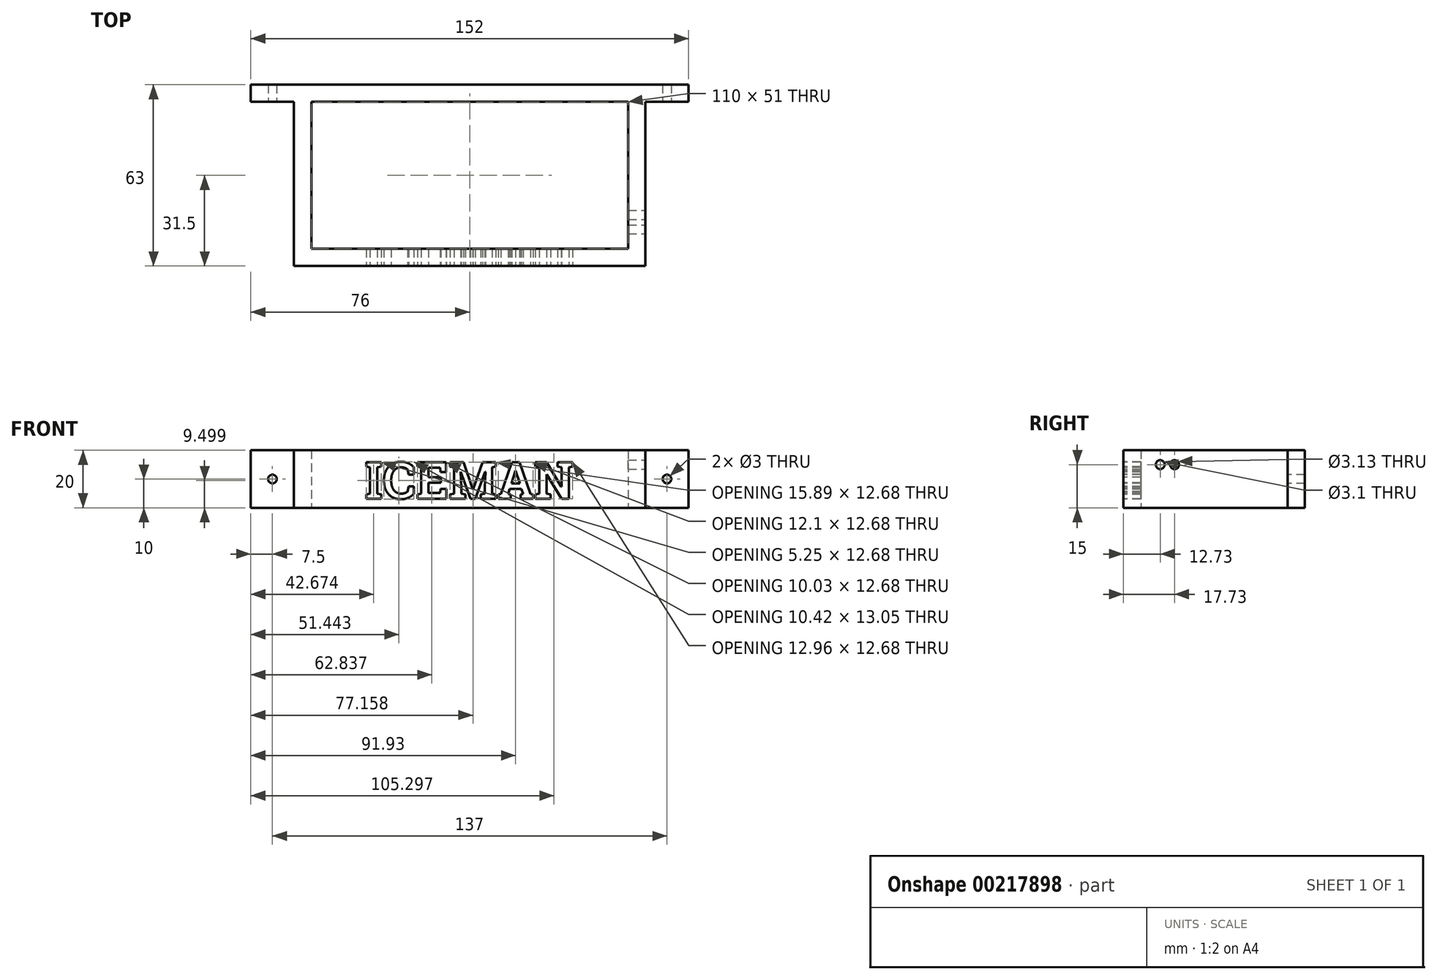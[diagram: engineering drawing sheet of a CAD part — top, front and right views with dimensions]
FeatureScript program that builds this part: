
annotation { "Feature Type Name" : "Feature", "Feature Type Description" : "" }
export const myFeature = defineFeature(function(context is Context, id is Id, definition is map)
    precondition{}
    {
        {
            var Q0;
            Q0=qCreatedBy(makeId("Top.planeOp"),FACE);
            var sketch = newSketch(context, id + "F0", { "sketchPlane" : qUnion([Q0])});
            skLineSegment(sketch, "E0.bottom", {"start": v(-61, 31.5) * mm, "end": v(61, 31.5) * mm});
            skLineSegment(sketch, "E0.top", {"start": v(-61, -31.5) * mm, "end": v(61, -31.5) * mm});
            skLineSegment(sketch, "E0.left", {"start": v(-61, 31.5) * mm, "end": v(-61, -31.5) * mm});
            skLineSegment(sketch, "E0.right", {"start": v(61, 31.5) * mm, "end": v(61, -31.5) * mm});
            skPoint(sketch, "E0.middle", {"position": v(0, 0) * mm});
            skSolve(sketch);
        }
        {
            var Q0;
            Q0=qSketchRegion(id+"F0",true);
            extrude(context, id + "F1", {"entities" : qUnion([Q0]), "depth" : 6 * mm});
        }
        {
            var Q0;
            Q0=makeQuery(id+"F1.opExtrude","CAP_FACE",FACE,{"disambiguationData":[OSD([sQuery(id+"F0.wireOp",EDGE,"E0.bottom"),sQuery(id+"F0.wireOp",EDGE,"E0.top"),sQuery(id+"F0.wireOp",EDGE,"E0.left"),sQuery(id+"F0.wireOp",EDGE,"E0.right")])],"isStart":false});
            var sketch = newSketch(context, id + "F2", { "sketchPlane" : qUnion([Q0])});
            skLineSegment(sketch, "E1", {"start": v(-55, 25.5) * mm, "end": v(-55, -25.5) * mm});
            skLineSegment(sketch, "E2", {"start": v(-55, -25.5) * mm, "end": v(55, -25.5) * mm});
            skLineSegment(sketch, "E3", {"start": v(55, 25.5) * mm, "end": v(-55, 25.5) * mm});
            skLineSegment(sketch, "E4", {"start": v(55, 25.5) * mm, "end": v(55, -25.5) * mm});
            skPoint(sketch, "E5.orphan", {"position": v(55, -31.5) * mm});
            skLineSegment(sketch, "E6.bottom", {"start": v(-61, 31.5) * mm, "end": v(61, 31.5) * mm});
            skLineSegment(sketch, "E6.top", {"start": v(-61, -31.5) * mm, "end": v(61, -31.5) * mm});
            skLineSegment(sketch, "E6.left", {"start": v(-61, 31.5) * mm, "end": v(-61, -31.5) * mm});
            skLineSegment(sketch, "E6.right", {"start": v(61, 31.5) * mm, "end": v(61, -31.5) * mm});
            skSolve(sketch);
        }
        {
            var Q0;
            Q0=qSketchRegion(id+"F2",true);
            extrude(context, id + "F3", {"entities" : qUnion([Q0]), "operationType" : NewBodyOperationType.ADD, "depth" : 66 * mm});
        }
        {
            var Q0;
            Q0=makeQuery(id+"F3.boolean.opBoolean","MERGE",FACE,{"derivedFrom":[makeQuery(id+"F1.opExtrude","SWEPT_FACE",FACE,{"disambiguationData":[OSD([sQuery(id+"F0.wireOp",EDGE,"E0.top")])]}),makeQuery(id+"F3.opExtrude","SWEPT_FACE",FACE,{"disambiguationData":[OSD([sQuery(id+"F2.wireOp",EDGE,"E6.top")])]})]});
            var sketch = newSketch(context, id + "F4", { "sketchPlane" : qUnion([Q0])});
            skLineSegment(sketch, "E7.bottom", {"start": v(48, 30.5) * mm, "end": v(20.38, 30.5) * mm});
            skLineSegment(sketch, "E7.top", {"start": v(48, 9) * mm, "end": v(20.38, 9) * mm});
            skLineSegment(sketch, "E7.left", {"start": v(48, 30.5) * mm, "end": v(48, 9) * mm});
            skLineSegment(sketch, "E7.right", {"start": v(20.38, 30.5) * mm, "end": v(20.38, 9) * mm});
            skLineSegment(sketch, "E8.bottom", {"start": v(-48, 30.5) * mm, "end": v(-21, 30.5) * mm});
            skLineSegment(sketch, "E8.top", {"start": v(-48, 12.5) * mm, "end": v(-21, 12.5) * mm});
            skLineSegment(sketch, "E8.left", {"start": v(-48, 30.5) * mm, "end": v(-48, 12.5) * mm});
            skLineSegment(sketch, "E8.right", {"start": v(-21, 30.5) * mm, "end": v(-21, 12.5) * mm});
            skText(sketch, "E9", { "text": "ICEMAN", "fontName": "RobotoSlab-Bold.ttf"});
            const initialGuessF4  = {"E9": [-0.03643, 0.04416, 1, 0, 0.01284]};
            skSetInitialGuess(sketch, initialGuessF4);
            skSolve(sketch);
        }
        {
            var Q0;
            Q0=qSketchRegion(id+"F4",true);
            extrude(context, id + "F5", {"entities" : qUnion([Q0]), "operationType" : NewBodyOperationType.REMOVE, "oppositeDirection" : true, "depth" : 6 * mm});
        }
        {
            var Q0;
            Q0=makeQuery(id+"F1.opExtrude","CAP_FACE",FACE,{"disambiguationData":[OSD([sQuery(id+"F0.wireOp",EDGE,"E0.bottom"),sQuery(id+"F0.wireOp",EDGE,"E0.top"),sQuery(id+"F0.wireOp",EDGE,"E0.left"),sQuery(id+"F0.wireOp",EDGE,"E0.right")])],"isStart":true});
            var sketch = newSketch(context, id + "F6", { "sketchPlane" : qUnion([Q0])});
            skPoint(sketch, "E10.bottom.start.orphan", {"position": v(42.45, 0) * mm});
            skText(sketch, "E11", { "text": "ICEMAN", "fontName": "OpenSans-BoldItalic.ttf"});
            const initialGuessF6  = {"E11": [-0.06005, -0.01114, 1, 0, 0.02254]};
            skSetInitialGuess(sketch, initialGuessF6);
            skSolve(sketch);
        }
        {
            var Q0;
            Q0=qSketchRegion(id+"F6",true);
            extrude(context, id + "F7", {"entities" : qUnion([Q0]), "operationType" : NewBodyOperationType.REMOVE, "oppositeDirection" : true, "depth" : 6 * mm});
        }
        {
            var Q0;
            Q0=makeQuery(id+"F3.boolean.opBoolean","MERGE",FACE,{"derivedFrom":[makeQuery(id+"F1.opExtrude","SWEPT_FACE",FACE,{"disambiguationData":[OSD([sQuery(id+"F0.wireOp",EDGE,"E0.right")])]}),makeQuery(id+"F3.opExtrude","SWEPT_FACE",FACE,{"disambiguationData":[OSD([sQuery(id+"F2.wireOp",EDGE,"E6.right")])]})]});
            var sketch = newSketch(context, id + "F8", { "sketchPlane" : qUnion([Q0])});
            skCircle(sketch, "E12", {"center": v(-18.77, 56) * mm, "radius": 1.55 * mm});
            skLineSegment(sketch, "E13", {"start": v(-18.77, 56) * mm, "end": v(33.66, 56) * mm, "construction": true});
            skCircle(sketch, "E14", {"center": v(-13.77, 56) * mm, "radius": 1.55 * mm, "construction": true});
            skCircle(sketch, "E15", {"center": v(-13.77, 56) * mm, "radius": 1.56 * mm});
            skSolve(sketch);
        }
        {
            var Q0;
            Q0=qSketchRegion(id+"F8",true);
            extrude(context, id + "F9", {"entities" : qUnion([Q0]), "operationType" : NewBodyOperationType.REMOVE, "oppositeDirection" : true, "depth" : 6 * mm});
        }
        {
            var Q0;
            Q0=makeQuery(id+"F3.boolean.opBoolean","MERGE",FACE,{"derivedFrom":[makeQuery(id+"F1.opExtrude","SWEPT_FACE",FACE,{"disambiguationData":[OSD([sQuery(id+"F0.wireOp",EDGE,"E0.right")])]}),makeQuery(id+"F3.opExtrude","SWEPT_FACE",FACE,{"disambiguationData":[OSD([sQuery(id+"F2.wireOp",EDGE,"E6.right")])]})]});
            var sketch = newSketch(context, id + "F10", { "sketchPlane" : qUnion([Q0])});
            skLineSegment(sketch, "E16.bottom", {"start": v(31.5, 61) * mm, "end": v(25.5, 61) * mm});
            skLineSegment(sketch, "E16.top", {"start": v(31.5, 41) * mm, "end": v(25.5, 41) * mm});
            skLineSegment(sketch, "E16.left", {"start": v(31.5, 61) * mm, "end": v(31.5, 41) * mm});
            skLineSegment(sketch, "E16.right", {"start": v(25.5, 61) * mm, "end": v(25.5, 41) * mm});
            skLineSegment(sketch, "E17", {"start": v(31.5, 61) * mm, "end": v(-91.25, 61) * mm, "construction": true});
            skLineSegment(sketch, "E18", {"start": v(-91.25, 61) * mm, "end": v(31.5, 41) * mm, "construction": true});
            skLineSegment(sketch, "E19", {"start": v(31.5, 41) * mm, "end": v(-54.22, 41) * mm, "construction": true});
            skLineSegment(sketch, "E20", {"start": v(-54.22, 41) * mm, "end": v(-136.07, 61) * mm, "construction": true});
            skSolve(sketch);
        }
        {
            var Q0;
            Q0=qSketchRegion(id+"F10",true);
            extrude(context, id + "F11", {"entities" : qUnion([Q0]), "operationType" : NewBodyOperationType.ADD, "depth" : 15 * mm});
        }
        {
            var Q0;
            Q0=makeQuery(id+"F3.boolean.opBoolean","MERGE",FACE,{"derivedFrom":[makeQuery(id+"F1.opExtrude","SWEPT_FACE",FACE,{"disambiguationData":[OSD([sQuery(id+"F0.wireOp",EDGE,"E0.left")])]}),makeQuery(id+"F3.opExtrude","SWEPT_FACE",FACE,{"disambiguationData":[OSD([sQuery(id+"F2.wireOp",EDGE,"E6.left")])]})]});
            var sketch = newSketch(context, id + "F12", { "sketchPlane" : qUnion([Q0])});
            skLineSegment(sketch, "E21.bottom", {"start": v(-31.5, 61) * mm, "end": v(-25.5, 61) * mm});
            skLineSegment(sketch, "E21.top", {"start": v(-31.5, 41) * mm, "end": v(-25.5, 41) * mm});
            skLineSegment(sketch, "E21.left", {"start": v(-31.5, 61) * mm, "end": v(-31.5, 41) * mm});
            skLineSegment(sketch, "E21.right", {"start": v(-25.5, 61) * mm, "end": v(-25.5, 41) * mm});
            skSolve(sketch);
        }
        {
            var Q0;
            Q0=qSketchRegion(id+"F12",true);
            extrude(context, id + "F13", {"entities" : qUnion([Q0]), "operationType" : NewBodyOperationType.ADD, "depth" : 15 * mm});
        }
        {
            var Q0;
            Q0=makeQuery(id+"F13.opExtrude","SWEPT_FACE",FACE,{"disambiguationData":[OSD([sQuery(id+"F12.wireOp",EDGE,"E21.right")])]});
            var sketch = newSketch(context, id + "F14", { "sketchPlane" : qUnion([Q0])});
            skCircle(sketch, "E22", {"center": v(-68.5, 51) * mm, "radius": 1.5 * mm});
            skPoint(sketch, "E22.centerSnap0", {"position": v(-68.5, 61) * mm});
            skPoint(sketch, "E22.centerSnap1", {"position": v(-76, 51) * mm});
            skSolve(sketch);
        }
        {
            var Q0;
            Q0=qSketchRegion(id+"F14",true);
            extrude(context, id + "F15", {"entities" : qUnion([Q0]), "operationType" : NewBodyOperationType.REMOVE, "endBound" : BoundingType.THROUGH_ALL, "oppositeDirection" : true, "depth" : 25 * mm});
        }
        {
            var Q0;
            Q0=makeQuery(id+"F11.opExtrude","SWEPT_FACE",FACE,{"disambiguationData":[OSD([sQuery(id+"F10.wireOp",EDGE,"E16.right")])]});
            var sketch = newSketch(context, id + "F16", { "sketchPlane" : qUnion([Q0])});
            skCircle(sketch, "E23", {"center": v(68.5, 51) * mm, "radius": 1.5 * mm});
            skPoint(sketch, "E23.centerSnap0", {"position": v(68.5, 61) * mm});
            skPoint(sketch, "E23.centerSnap1", {"position": v(76, 51) * mm});
            skSolve(sketch);
        }
        {
            var Q0;
            Q0=qSketchRegion(id+"F16",true);
            extrude(context, id + "F17", {"entities" : qUnion([Q0]), "operationType" : NewBodyOperationType.ADD, "endBound" : BoundingType.THROUGH_ALL, "depth" : 25 * mm});
        }
        {
            var Q0;
            Q0=makeQuery(id+"F17.opExtrude","CAP_FACE",FACE,{"disambiguationData":[OSD([sQuery(id+"F16.wireOp",EDGE,"E23")])],"isStart":false});
            extrude(context, id + "F18", {"entities" : qUnion([Q0]), "operationType" : NewBodyOperationType.REMOVE, "endBound" : BoundingType.THROUGH_ALL, "oppositeDirection" : true, "depth" : 25 * mm});
        }
        {
            var Q0;
            Q0=makeQuery(id+"F13.opExtrude","SWEPT_FACE",FACE,{"disambiguationData":[OSD([sQuery(id+"F12.wireOp",EDGE,"E21.right")])]});
            var sketch = newSketch(context, id + "F19", { "sketchPlane" : qUnion([Q0])});
            skLineSegment(sketch, "E24.bottom", {"start": v(-76, 41) * mm, "end": v(76.84, 41) * mm});
            skLineSegment(sketch, "E24.top", {"start": v(-76, -5) * mm, "end": v(76.84, -5) * mm});
            skLineSegment(sketch, "E24.left", {"start": v(-76, 41) * mm, "end": v(-76, -5) * mm});
            skLineSegment(sketch, "E24.right", {"start": v(76.84, 41) * mm, "end": v(76.84, -5) * mm});
            skLineSegment(sketch, "E25.bottom", {"start": v(-76, 61) * mm, "end": v(78.57, 61) * mm});
            skLineSegment(sketch, "E25.top", {"start": v(-76, 73.41) * mm, "end": v(78.57, 73.41) * mm});
            skLineSegment(sketch, "E25.left", {"start": v(-76, 61) * mm, "end": v(-76, 73.41) * mm});
            skLineSegment(sketch, "E25.right", {"start": v(78.57, 61) * mm, "end": v(78.57, 73.41) * mm});
            skSolve(sketch);
        }
        {
            var Q0;
            Q0=makeQuery(id+"F19.imprint","IMPRINT",FACE,{"disambiguationData":[TD([[makeQuery(id+"F19.imprint","IMPRINT",EDGE,{"derivedFrom":sQuery(id+"F19.wireOp",EDGE,"E24.top")}),1.0]])]});
            var Q1;
            Q1=makeQuery(id+"F19.imprint","IMPRINT",FACE,{"disambiguationData":[TD([[makeQuery(id+"F19.imprint","IMPRINT",EDGE,{"derivedFrom":sQuery(id+"F19.wireOp",EDGE,"E25.top")}),-1.0]])]});
            extrude(context, id + "F20", {"entities" : qUnion([Q0, Q1]), "operationType" : NewBodyOperationType.REMOVE, "endBound" : BoundingType.THROUGH_ALL, "depth" : 25 * mm, "hasSecondDirection" : true, "secondDirectionBound" : SecondDirectionBoundingType.THROUGH_ALL, "secondDirectionOppositeDirection" : true, "secondDirectionDepth" : 25 * mm});
        }
    });
